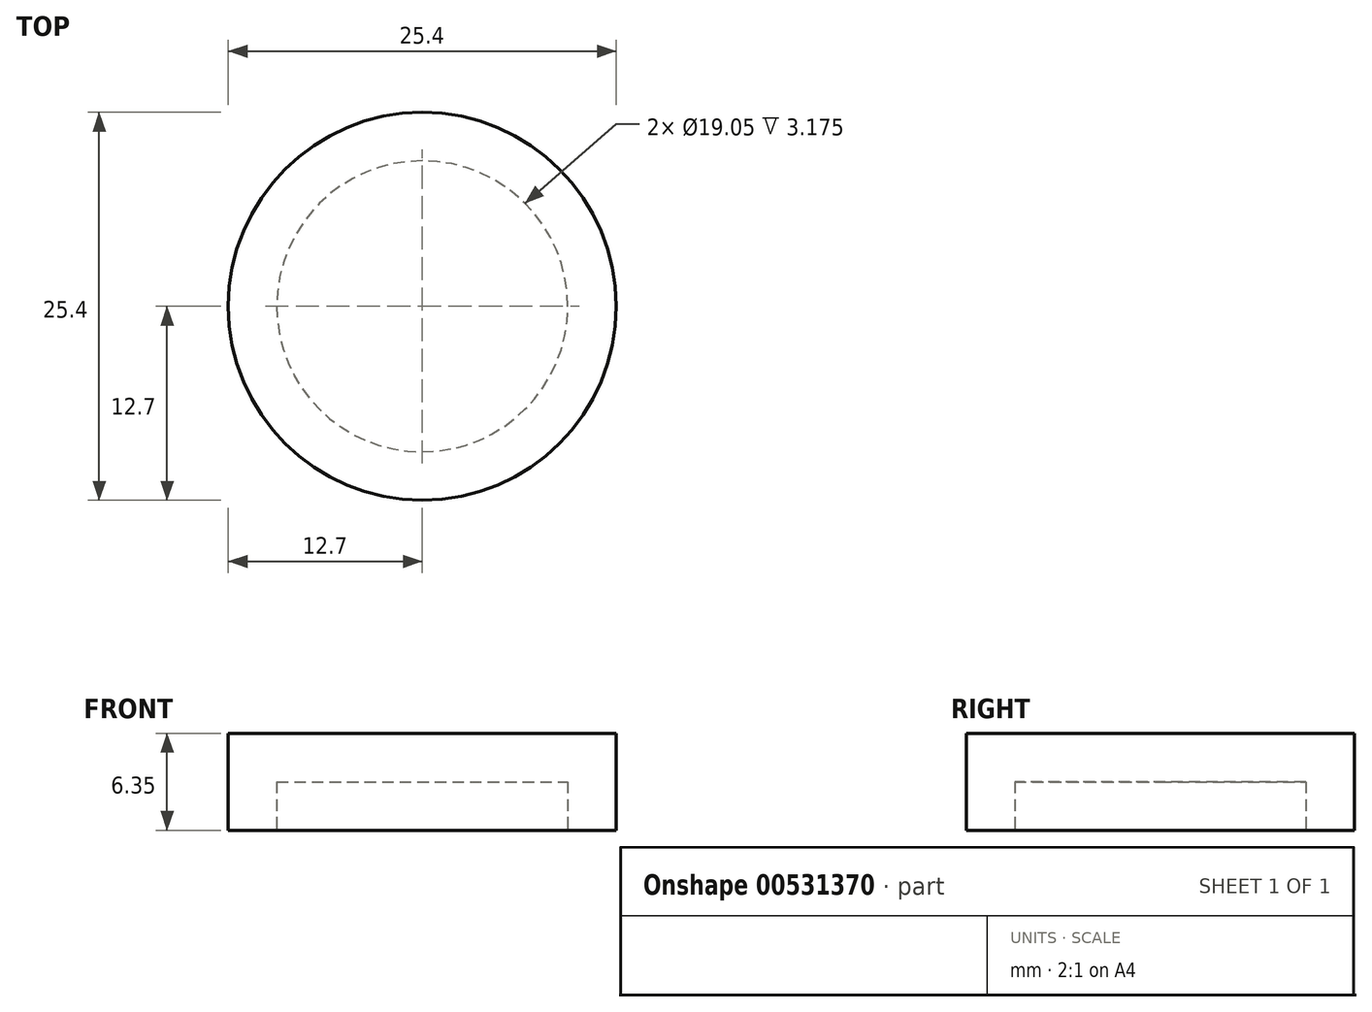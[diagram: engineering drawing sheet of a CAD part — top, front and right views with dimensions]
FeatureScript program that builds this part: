
annotation { "Feature Type Name" : "Feature", "Feature Type Description" : "" }
export const myFeature = defineFeature(function(context is Context, id is Id, definition is map)
    precondition{}
    {
        {
            var Q0;
            Q0=qCreatedBy(makeId("Front.planeOp"),FACE);
            var sketch = newSketch(context, id + "F0", { "sketchPlane" : qUnion([Q0])});
            skLineSegment(sketch, "E0", {"start": v(0, 0) * mm, "end": v(12.7, 0) * mm});
            skLineSegment(sketch, "E1", {"start": v(12.7, 0) * mm, "end": v(12.7, -6.35) * mm});
            skLineSegment(sketch, "E2", {"start": v(12.7, -6.35) * mm, "end": v(9.53, -6.35) * mm});
            skLineSegment(sketch, "E3", {"start": v(9.53, -6.35) * mm, "end": v(9.53, -3.18) * mm});
            skLineSegment(sketch, "E4", {"start": v(9.53, -3.18) * mm, "end": v(0, -3.18) * mm});
            skLineSegment(sketch, "E5", {"start": v(0, -3.18) * mm, "end": v(0, 0) * mm});
            skSolve(sketch);
        }
        {
            var Q0;
            Q0 = qSketchRegion(id + "F0", true);
            var Q1;
            Q1=sQuery(id+"F0.wireOp",EDGE,"E5");
            revolve(context, id + "F1", {"entities" : qUnion([Q0]), "axis" : qUnion([Q1]), "revolveType" : RevolveType.FULL});
        }
    });
